# Revit family: Active Climbing Net 4000
name_source: partatom
category: Furniture
units: mm (PartAtom-declared; Revit-internal decimal feet)

## family parameters
Always vertical = Yes
Cut with Voids When Loaded = No
OmniClass Number = 23.21.23.13.15
Room Calculation Point = No
Shared = No
Work Plane-Based = No

## types (2) — shared parameters
BIMobject category = Climbers
Body material_10 = Hags - Rope - Black
Construction material = Hags - Steel
Description = Active Climbing Net 4000
Edition number = 1
IFC Classification = Play Equipment
Manufacturer = Hags
Manufacturer name = HAGS
OmniClass Code = 23-21 23 13 15
OmniClass Description = Playground Equipment
Product name = Active Climbing Net 4000
Product url = https://www.hags.com
URL = https://www.hags.com
Uniclass 1.4 Code = L8211
Uniclass 1.4 Description = Play Equipment
zero-valued in all types: Default Elevation

## per-type parameters (varying)
| type | Body material_20 | Model |
| 8074808 Green/ Black | Hags - Rope - Green | 8074808 |
| 8074809 Red/ Black | Hags - Rope - Red | 8074809 |

## geometry (parser evidence)
native form markers: Sweep x3
no freeform markers — native parametric forms only
